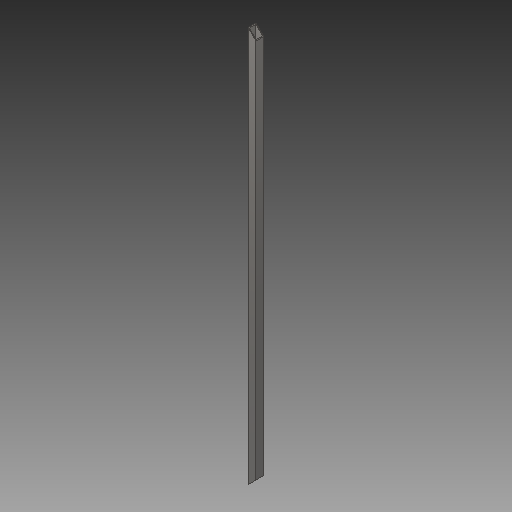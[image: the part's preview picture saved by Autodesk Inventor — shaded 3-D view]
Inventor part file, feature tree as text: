
AUTODESK INVENTOR PART (.ipt)
format: ipt  version: 2019 (Build 230136000, 136)  size: 102,400 bytes
history: native  units: mm
features: other x3, sketch x2
ambient origin geometry x8: Origin, YZ Plane, XZ Plane, XY Plane, X Axis, Y Axis, Z Axis, Center Point
bodies: Solid1 (feature_tree)
feature tree (5):
  other  "1500mm_box_section.ipt"
  other  "Solid1::1500mm_box_section.ipt"
  other  "TaggingFeature1"
  sketch  "Sketch1"  dims[d0=10.0mm]
  sketch  "Sketch2"
